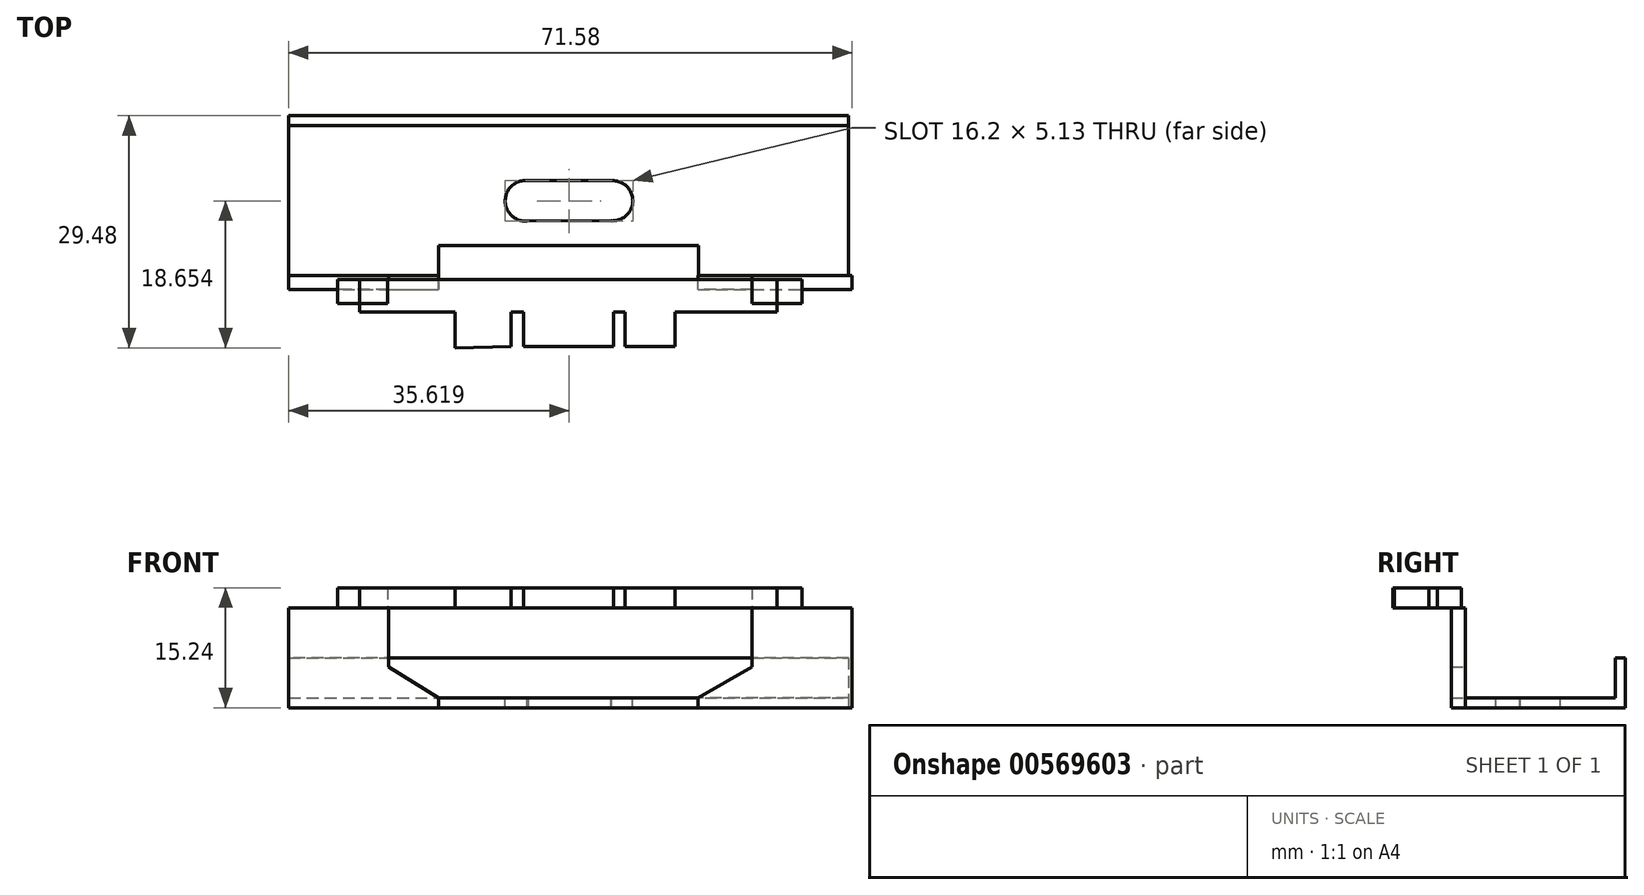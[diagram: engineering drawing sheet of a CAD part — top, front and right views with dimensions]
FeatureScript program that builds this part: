
annotation { "Feature Type Name" : "Feature", "Feature Type Description" : "" }
export const myFeature = defineFeature(function(context is Context, id is Id, definition is map)
    precondition{}
    {
        {
            var Q0;
            Q0=qCreatedBy(makeId("Top.planeOp"),FACE);
            var sketch = newSketch(context, id + "F0", { "sketchPlane" : qUnion([Q0])});
            skLineSegment(sketch, "E0.bottom", {"start": v(35.56, -8.25) * mm, "end": v(-35.56, -8.26) * mm});
            skLineSegment(sketch, "E0.top", {"start": v(35.56, 8.26) * mm, "end": v(-35.56, 8.25) * mm});
            skLineSegment(sketch, "E0.left", {"start": v(35.56, -8.25) * mm, "end": v(35.56, 8.26) * mm});
            skLineSegment(sketch, "E0.right", {"start": v(-35.56, -8.26) * mm, "end": v(-35.56, 8.25) * mm});
            skPoint(sketch, "E0.middle", {"position": v(0, 0) * mm});
            skLineSegment(sketch, "E1.bottom", {"start": v(-35.56, -8.26) * mm, "end": v(-16.51, -8.26) * mm});
            skLineSegment(sketch, "E1.top", {"start": v(-35.56, -12.07) * mm, "end": v(-16.51, -12.07) * mm});
            skLineSegment(sketch, "E1.left", {"start": v(-35.56, -8.26) * mm, "end": v(-35.56, -12.07) * mm});
            skLineSegment(sketch, "E1.right", {"start": v(-16.51, -8.26) * mm, "end": v(-16.51, -12.06) * mm});
            skLineSegment(sketch, "E2.bottom", {"start": v(35.56, -8.25) * mm, "end": v(16.51, -8.25) * mm});
            skLineSegment(sketch, "E2.top", {"start": v(35.56, -12.07) * mm, "end": v(16.51, -12.07) * mm});
            skLineSegment(sketch, "E2.left", {"start": v(35.56, -8.25) * mm, "end": v(35.56, -12.07) * mm});
            skLineSegment(sketch, "E2.right", {"start": v(16.51, -8.25) * mm, "end": v(16.51, -12.06) * mm});
            skSolve(sketch);
        }
        {
            var Q0;
            Q0 = qSketchRegion(id + "F0", true);
            extrude(context, id + "F1", {"entities" : qUnion([Q0]), "depth" : 1.27 * mm, "offsetDistance" : 25.4 * mm});
        }
        {
            var Q0;
            Q0=makeQuery(id+"F1.opExtrude","CAP_FACE",FACE,{"disambiguationData":[OSD([sQuery(id+"F0.wireOp",EDGE,"E0.bottom"),sQuery(id+"F0.wireOp",EDGE,"E0.top"),sQuery(id+"F0.wireOp",EDGE,"E0.left"),sQuery(id+"F0.wireOp",EDGE,"E0.right")])],"isStart":false});
            var sketch = newSketch(context, id + "F2", { "sketchPlane" : qUnion([Q0])});
            skPoint(sketch, "E3.endSnap0", {"position": v(3.18, 0) * mm});
            skLineSegment(sketch, "E4", {"start": v(6.35, -5.08) * mm, "end": v(6.35, 0) * mm});
            skLineSegment(sketch, "E5", {"start": v(-6.35, -5.08) * mm, "end": v(-6.35, 0) * mm});
            skArc(sketch, "E6", {"start": v(5.35, -5.08) * mm, "mid": v(8.16, -2.6) * mm, "end": v(5.44, 0) * mm});
            skArc(sketch, "E7", {"start": v(-5.06, 0) * mm, "mid": v(-8.04, -2.63) * mm, "end": v(-4.91, -5.08) * mm});
            skLineSegment(sketch, "E8", {"start": v(-5.06, 0) * mm, "end": v(5.44, 0) * mm});
            skLineSegment(sketch, "E9", {"start": v(-5.6, -5.13) * mm, "end": v(5.88, -5.08) * mm});
            skSolve(sketch);
        }
        {
            var Q0;
            Q0 = qSketchRegion(id + "F2", true);
            extrude(context, id + "F3", {"entities" : qUnion([Q0]), "operationType" : NewBodyOperationType.REMOVE, "oppositeDirection" : true, "depth" : 25.4 * mm, "offsetDistance" : 25.4 * mm});
        }
        {
            var Q0;
            Q0=makeQuery(id+"F1.opExtrude","CAP_FACE",FACE,{"disambiguationData":[OSD([sQuery(id+"F0.wireOp",EDGE,"E0.bottom"),sQuery(id+"F0.wireOp",EDGE,"E0.top"),sQuery(id+"F0.wireOp",EDGE,"E0.left"),sQuery(id+"F0.wireOp",EDGE,"E0.right"),sQuery(id+"F0.wireOp",EDGE,"E1.top"),sQuery(id+"F0.wireOp",EDGE,"E1.left"),sQuery(id+"F0.wireOp",EDGE,"E1.right"),sQuery(id+"F0.wireOp",EDGE,"E2.top"),sQuery(id+"F0.wireOp",EDGE,"E2.left"),sQuery(id+"F0.wireOp",EDGE,"E2.right")])],"isStart":false});
            var sketch = newSketch(context, id + "F4", { "sketchPlane" : qUnion([Q0])});
            skLineSegment(sketch, "E10.bottom", {"start": v(-35.56, 8.25) * mm, "end": v(35.56, 8.25) * mm});
            skLineSegment(sketch, "E10.top", {"start": v(-35.56, 6.98) * mm, "end": v(35.56, 6.98) * mm});
            skLineSegment(sketch, "E10.left", {"start": v(-35.56, 8.25) * mm, "end": v(-35.56, 6.98) * mm});
            skLineSegment(sketch, "E10.right", {"start": v(35.56, 8.25) * mm, "end": v(35.56, 6.98) * mm});
            skSolve(sketch);
        }
        {
            var Q0;
            Q0 = qSketchRegion(id + "F4", true);
            extrude(context, id + "F5", {"entities" : qUnion([Q0]), "operationType" : NewBodyOperationType.ADD, "depth" : 5.08 * mm, "offsetDistance" : 25.4 * mm});
        }
        {
            var Q0;
            Q0=makeQuery(id+"F1.opExtrude","SWEPT_FACE",FACE,{"disambiguationData":[OSD([sQuery(id+"F0.wireOp",EDGE,"E1.top")])]});
            var sketch = newSketch(context, id + "F6", { "sketchPlane" : qUnion([Q0])});
            skLineSegment(sketch, "E11", {"start": v(-35.56, 0) * mm, "end": v(-35.56, 12.71) * mm});
            skLineSegment(sketch, "E12", {"start": v(-35.56, 12.71) * mm, "end": v(-22.86, 12.71) * mm});
            skLineSegment(sketch, "E13", {"start": v(-22.86, 12.71) * mm, "end": v(-22.86, 5.22) * mm});
            skLineSegment(sketch, "E14", {"start": v(-22.86, 5.22) * mm, "end": v(-16.51, 1.27) * mm});
            skLineSegment(sketch, "E15", {"start": v(36.02, 0) * mm, "end": v(36.02, 12.7) * mm});
            skLineSegment(sketch, "E16", {"start": v(36.02, 12.7) * mm, "end": v(23.32, 12.7) * mm});
            skLineSegment(sketch, "E17", {"start": v(23.32, 12.7) * mm, "end": v(23.32, 5.21) * mm});
            skLineSegment(sketch, "E18", {"start": v(23.32, 5.21) * mm, "end": v(16.42, 1.27) * mm});
            skLineSegment(sketch, "E19", {"start": v(-35.56, 0) * mm, "end": v(-16.51, 0) * mm});
            skLineSegment(sketch, "E20", {"start": v(-16.51, 0) * mm, "end": v(-16.51, 1.27) * mm});
            skLineSegment(sketch, "E21", {"start": v(16.42, 1.27) * mm, "end": v(16.42, 0) * mm});
            skLineSegment(sketch, "E22", {"start": v(16.42, 0) * mm, "end": v(36.02, 0) * mm});
            skSolve(sketch);
        }
        {
            var Q0;
            Q0 = qSketchRegion(id + "F6", true);
            extrude(context, id + "F7", {"entities" : qUnion([Q0]), "operationType" : NewBodyOperationType.ADD, "depth" : 1.78 * mm, "offsetDistance" : 25.4 * mm});
        }
        {
            var Q0;
            Q0=makeQuery(id+"F7.opExtrude","SWEPT_FACE",FACE,{"disambiguationData":[OSD([sQuery(id+"F6.wireOp",EDGE,"E16")])]});
            var sketch = newSketch(context, id + "F8", { "sketchPlane" : qUnion([Q0])});
            skLineSegment(sketch, "E23.bottom", {"start": v(29.67, -12.57) * mm, "end": v(23.32, -12.57) * mm});
            skLineSegment(sketch, "E23.top", {"start": v(29.67, -15.62) * mm, "end": v(23.32, -15.62) * mm});
            skLineSegment(sketch, "E23.left", {"start": v(29.67, -12.57) * mm, "end": v(29.67, -15.62) * mm});
            skLineSegment(sketch, "E23.right", {"start": v(23.32, -12.57) * mm, "end": v(23.32, -15.62) * mm});
            skLineSegment(sketch, "E24.bottom", {"start": v(-29.32, -12.57) * mm, "end": v(-22.97, -12.57) * mm});
            skLineSegment(sketch, "E24.top", {"start": v(-29.32, -15.62) * mm, "end": v(-22.97, -15.62) * mm});
            skLineSegment(sketch, "E24.left", {"start": v(-29.32, -12.57) * mm, "end": v(-29.32, -15.62) * mm});
            skLineSegment(sketch, "E24.right", {"start": v(-22.97, -12.57) * mm, "end": v(-22.97, -15.62) * mm});
            skSolve(sketch);
        }
        {
            var Q0;
            Q0 = qSketchRegion(id + "F8", true);
            extrude(context, id + "F9", {"entities" : qUnion([Q0]), "operationType" : NewBodyOperationType.ADD, "depth" : 2.54 * mm, "offsetDistance" : 25.4 * mm});
        }
        {
            var Q0;
            Q0=makeQuery(id+"F9.opExtrude","CAP_FACE",FACE,{"disambiguationData":[OSD([sQuery(id+"F8.wireOp",EDGE,"E23.bottom"),sQuery(id+"F8.wireOp",EDGE,"E23.top"),sQuery(id+"F8.wireOp",EDGE,"E23.left"),sQuery(id+"F8.wireOp",EDGE,"E23.right")])],"isStart":true});
            var sketch = newSketch(context, id + "F10", { "sketchPlane" : qUnion([Q0])});
            skLineSegment(sketch, "E25", {"start": v(26.5, 12.57) * mm, "end": v(-26.51, 12.57) * mm});
            skLineSegment(sketch, "E26", {"start": v(-26.51, 12.57) * mm, "end": v(-26.51, 16.67) * mm});
            skLineSegment(sketch, "E27", {"start": v(-26.51, 16.67) * mm, "end": v(26.5, 16.67) * mm});
            skPoint(sketch, "E27.endSnap0", {"position": v(26.5, 15.62) * mm});
            skLineSegment(sketch, "E28", {"start": v(26.5, 16.67) * mm, "end": v(26.5, 12.57) * mm});
            skLineSegment(sketch, "E29.bottom", {"start": v(-5.72, 21.08) * mm, "end": v(5.71, 21.08) * mm});
            skLineSegment(sketch, "E29.top", {"start": v(-5.72, 14.54) * mm, "end": v(5.71, 14.54) * mm});
            skLineSegment(sketch, "E29.left", {"start": v(-5.72, 21.08) * mm, "end": v(-5.72, 14.54) * mm});
            skLineSegment(sketch, "E29.right", {"start": v(5.72, 21.08) * mm, "end": v(5.71, 14.54) * mm});
            skPoint(sketch, "E29.middle", {"position": v(0, 17.8) * mm});
            skLineSegment(sketch, "E30.bottom", {"start": v(7.2, 14.54) * mm, "end": v(13.55, 14.54) * mm});
            skLineSegment(sketch, "E30.top", {"start": v(7.2, 21.08) * mm, "end": v(13.55, 21.08) * mm});
            skLineSegment(sketch, "E30.left", {"start": v(7.2, 14.54) * mm, "end": v(7.2, 21.08) * mm});
            skLineSegment(sketch, "E30.right", {"start": v(13.55, 14.54) * mm, "end": v(13.55, 21.08) * mm});
            skLineSegment(sketch, "E31.right", {"start": v(-14.42, 14.54) * mm, "end": v(-14.42, 21.22) * mm});
            skLineSegment(sketch, "E32", {"start": v(-14.42, 21.22) * mm, "end": v(-7.32, 21.08) * mm});
            skLineSegment(sketch, "E33", {"start": v(-7.32, 21.08) * mm, "end": v(-7.32, 14.42) * mm});
            skLineSegment(sketch, "E34", {"start": v(-7.32, 14.42) * mm, "end": v(-14.42, 14.54) * mm});
            skSolve(sketch);
        }
        {
            var Q0;
            Q0 = qSketchRegion(id + "F10", true);
            extrude(context, id + "F11", {"entities" : qUnion([Q0]), "oppositeDirection" : true, "depth" : 2.54 * mm, "offsetDistance" : 25.4 * mm});
        }
    });
